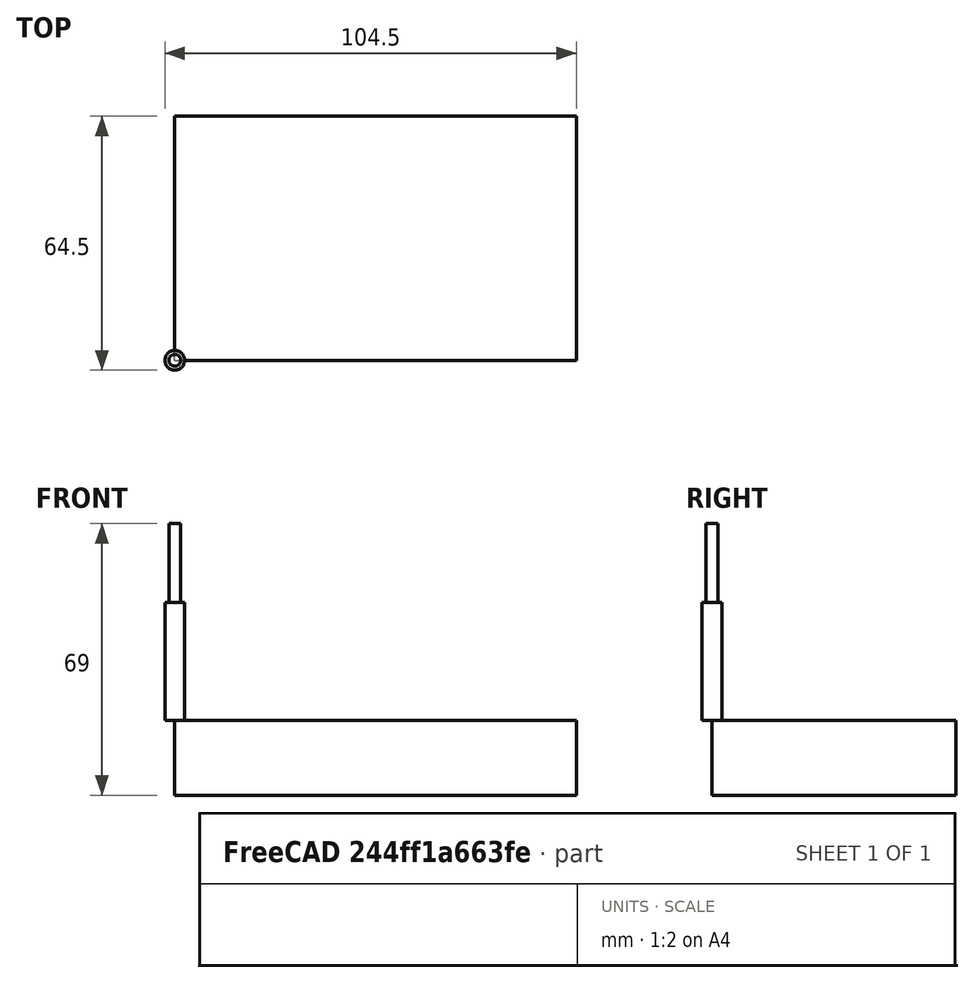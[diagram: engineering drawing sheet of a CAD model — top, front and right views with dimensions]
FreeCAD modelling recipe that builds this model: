
FCSTD DOCUMENT  (FreeCAD 0.19R23546 (Git))
Label: Cylindres25mmx19mmX2
License: All rights reserved
LicenseURL: http://en.wikipedia.org/wiki/All_rights_reserved
objects: Path::FeaturePython×6, Part::FeaturePython×3, Sketcher::SketchObject×2, PartDesign::Pad×1, PartDesign::Pocket×1, PartDesign::Body×1, App::FeaturePython×1, App::DocumentObjectGroup×1, Path::FeatureCompoundPython×1, Mesh::FeaturePython×1
note: 12 computed .brp shape members not serialized (recipe doc carries the construction recipe); baked Part::Feature solids carry a one-line shape summary decoded from their .brp

FEATURE [Sketcher::SketchObject] Sketch
  MapMode = 5
  Support = -> [XY_Plane]
  sketch-geometry (4):
    g0: LineSegment StartX=0 StartY=60 StartZ=0 EndX=100 EndY=60 EndZ=0
    g1: LineSegment StartX=100 StartY=60 StartZ=0 EndX=100 EndY=0 EndZ=0
    g2: LineSegment StartX=100 StartY=0 StartZ=0 EndX=0 EndY=0 EndZ=0
    g3: LineSegment StartX=0 StartY=0 StartZ=0 EndX=0 EndY=60 EndZ=0
  constraints (10):
    c: Coincident(g0,g1)
    c: Coincident(g1,g2)
    c: Coincident(g2,g3)
    c: Coincident(g3,g0)
    c: Horizontal(g0)
    c: Horizontal(g2)
    c: Vertical(g1)
    c: Vertical(g3)
    c: PointOnObject(g0,g-2)
    c: PointOnObject(g1,g-1)
FEATURE [PartDesign::Pad] Pad
  Direction = (1,1,1)
  Length = 19
  Length2 = 100
  Profile = -> Sketch
  Type = 0
FEATURE [Sketcher::SketchObject] Sketch001
  MapMode = 5
  Placement = pos=(0,0,19) rot=(0,0,1;0rad)
  Support = -> [Pad]
  sketch-geometry (2):
    g0: Circle CenterX=25 CenterY=30 CenterZ=0 NormalX=0 NormalY=0 NormalZ=1 AngleXU=0 Radius=18.5
    g1: Circle CenterX=75 CenterY=30 CenterZ=0 NormalX=0 NormalY=0 NormalZ=1 AngleXU=0 Radius=18.5
  constraints (4):
    c: DistanceX(g-1,g0) = 25
    c: Diameter(g0) = 37
    c: DistanceX(g-1,g1) = 75
    c: Diameter(g1) = 37
FEATURE [PartDesign::Pocket] Pocket
  BaseFeature = -> Pad
  Length = 5
  Length2 = 100
  Profile = -> Sketch001
  Type = 1
FEATURE [PartDesign::Body] Body
  Group = -> [Sketch,Pad,Sketch001,Pocket]
  Origin = -> Origin
  Tip = -> Pocket
FEATURE [App::FeaturePython] SetupSheet  # Path/CAM operation (typed FeaturePython)
  ClearanceHeightExpression = OpStockZMax+SetupSheet.ClearanceHeightOffset
  ClearanceHeightOffset = 5
  CoolantMode = 0
  CoolantModes = None | Flood | Mist
  FinalDepthExpression = OpFinalDepth
  HorizRapid = 0
  SafeHeightExpression = OpStockZMax+SetupSheet.SafeHeightOffset
  SafeHeightOffset = 3
  StartDepthExpression = OpStartDepth
  StepDownExpression = OpToolDiameter
  VertRapid = 0
FEATURE [Part::FeaturePython] Clone  label="Model-Body"  # Draft clone (typed FeaturePython)
  AttacherType = Attacher::AttachEngine3D
  Fuse = false
  Objects = -> [Body]
  PathResource = Model
  Placement = pos=(1,1,-19) rot=(0,0,1;0rad)
  Scale = (1,1,1)
FEATURE [App::DocumentObjectGroup] Model
  Group = -> [Clone]
FEATURE [Part::FeaturePython] ToolBit  label="Endmill"  # Path/CAM toolbit (typed FeaturePython)
  BitShape = <path>
  CuttingEdgeHeight = 30
  Diameter = 6
  Length = 50
  ShankDiameter = 3
  ShapeName = endmill
FEATURE [Path::FeaturePython] TC__Default_Tool  label="TC: Default Tool"  # Path/CAM operation (typed FeaturePython)
  HorizFeed = 0
  HorizRapid = 0
  SpindleDir = 0
  SpindleSpeed = 0
  Tool = -> ToolBit
  ToolNumber = 1
  VertFeed = 0
  VertRapid = 0
  expr: VertRapid = SetupSheet.VertRapid
  expr: HorizRapid = SetupSheet.HorizRapid
FEATURE [Part::FeaturePython] Stock  # WARN: FeaturePython — macro-defined, semantics opaque (R4)
  Base = -> Model
  ExtXneg = 1
  ExtXpos = 1
  ExtYneg = 1
  ExtYpos = 1
  ExtZneg = 0
  ExtZpos = 0
  Placement = pos=(1,1,-19) rot=(0,0,1;0rad)
  StockType = FromBase
FEATURE [Path::FeaturePython] Profile  # Path/CAM operation (typed FeaturePython)
  Active = true
  AreaParams:
    Tolerance = 1e-07
    FitArcs = True
    Simplify = False
    CleanDistance = 0.0
    Accuracy = 0.01
    Unit = 1.0
    MinArcPoints = 4
    MaxArcPoints = 100
    ClipperScale = 10000000.0
    Fill = 0
    Coplanar = 0
    Reorient = True
    Outline = False
    Explode = False
    OpenMode = 0
    Deflection = 0.01
    SubjectFill = 0
    ClipFill = 0
    Offset = -3.0
    ExtraPass = 0
    Stepover = 0.0
    LastStepover = 0.0
    JoinType = 0
    EndType = 0
    MiterLimit = 2.0
    RoundPrecision = 0.0
    PocketMode = 0
    ToolRadius = 1.0
    PocketExtraOffset = 0.0
    PocketStepover = 0.0
    PocketLastStepover = 0.0
    FromCenter = False
    Angle = 45.0
    AngleShift = 0.0
    Shift = 0.0
    Thicken = False
    SectionCount = -1
    Stepdown = 1.0
    SectionOffset = 0.0
    SectionTolerance = 1e-06
    SectionMode = 2
    Project = False
  AttemptInverseAngle = true
  Base = -> [Clone]
  ClearanceHeight = 5
  CoolantMode = None
  CycleTime = Erreur de temps de cycle
  Direction = 1
  EnableRotation = 0
  ExpandProfile = 0
  ExpandProfileStepOver = 100
  FinalDepth = -19
  HandleMultipleFeatures = 1
  InverseAngle = false
  JoinType = 0
  LimitDepthToFace = true
  MiterLimit = 0.1
  OffsetExtra = 0
  OpFinalDepth = -19
  OpStartDepth = 0
  OpStockZMax = 0
  OpStockZMin = -19
  OpToolDiameter = 6
  PathParams = {'orientation': 0, 'feedrate': 0.0, 'feedrate_v': 0.0, 'verbose': True, 'resume_height': 3.0, 'retraction': 5.0, 'return_end': True, 'preamble': False, 'start': Vector (0.0, 0.0, 0.0)}
  ReverseDirection = false
  SafeHeight = 3
  Side = 1
  StartDepth = 0
  StartPoint = (0,0,0)
  StepDown = 3
  ToolController = -> TC__Default_Tool
  UseComp = true
  UseStartPoint = true
  processCircles = false
  processHoles = false
  processPerimeter = true
  expr: StartDepth = OpStartDepth
  expr: FinalDepth = OpFinalDepth
  expr: StepDown = 3
  expr: SafeHeight = OpStockZMax + SetupSheet.SafeHeightOffset
  expr: ClearanceHeight = OpStockZMax + SetupSheet.ClearanceHeightOffset
FEATURE [Path::FeaturePython] DressupTag  # Path/CAM operation (typed FeaturePython)
  Angle = 45
  Base = -> Profile
  Height = 9.5
  Positions = (4) [(15.9082,42.7625,0),(11.1697,26.4985,0),(38.2957,21.5652,0),(35.4348,43.2957,0)]
  Radius = 0
  SegmentationFactor = 50
  Width = 3.58
FEATURE [Path::FeaturePython] Profile001  # Path/CAM operation (typed FeaturePython)
  Active = true
  AreaParams:
    Tolerance = 1e-07
    FitArcs = True
    Simplify = False
    CleanDistance = 0.0
    Accuracy = 0.01
    Unit = 1.0
    MinArcPoints = 4
    MaxArcPoints = 100
    ClipperScale = 10000000.0
    Fill = 0
    Coplanar = 0
    Reorient = True
    Outline = False
    Explode = False
    OpenMode = 0
    Deflection = 0.01
    SubjectFill = 0
    ClipFill = 0
    Offset = -3.0
    ExtraPass = 0
    Stepover = 0.0
    LastStepover = 0.0
    JoinType = 0
    EndType = 0
    MiterLimit = 2.0
    RoundPrecision = 0.0
    PocketMode = 0
    ToolRadius = 1.0
    PocketExtraOffset = 0.0
    PocketStepover = 0.0
    PocketLastStepover = 0.0
    FromCenter = False
    Angle = 45.0
    AngleShift = 0.0
    Shift = 0.0
    Thicken = False
    SectionCount = -1
    Stepdown = 1.0
    SectionOffset = 0.0
    SectionTolerance = 1e-06
    SectionMode = 2
    Project = False
  AttemptInverseAngle = true
  Base = -> [Clone]
  ClearanceHeight = 5
  CoolantMode = None
  CycleTime = Erreur de temps de cycle
  Direction = 1
  EnableRotation = 0
  ExpandProfile = 0
  ExpandProfileStepOver = 100
  FinalDepth = -19
  HandleMultipleFeatures = 1
  InverseAngle = false
  JoinType = 0
  LimitDepthToFace = true
  MiterLimit = 0.1
  OffsetExtra = 0
  OpFinalDepth = -19
  OpStartDepth = 0
  OpStockZMax = 0
  OpStockZMin = -19
  OpToolDiameter = 6
  PathParams = {'orientation': 0, 'feedrate': 0.0, 'feedrate_v': 0.0, 'verbose': True, 'resume_height': 3.0, 'retraction': 5.0, 'return_end': True, 'preamble': False, 'start': Vector (0.0, 0.0, 0.0)}
  ReverseDirection = false
  SafeHeight = 3
  Side = 1
  StartDepth = 0
  StartPoint = (0,0,0)
  StepDown = 3
  ToolController = -> TC__Default_Tool
  UseComp = true
  UseStartPoint = true
  processCircles = false
  processHoles = false
  processPerimeter = true
  expr: StartDepth = OpStartDepth
  expr: FinalDepth = OpFinalDepth
  expr: StepDown = 3
  expr: SafeHeight = OpStockZMax + SetupSheet.SafeHeightOffset
  expr: ClearanceHeight = OpStockZMax + SetupSheet.ClearanceHeightOffset
FEATURE [Path::FeaturePython] DressupTag001  # Path/CAM operation (typed FeaturePython)
  Angle = 45
  Base = -> Profile001
  Height = 9.5
  Positions = (4) [(62.599,38.7854,0),(68.2146,17.599,0),(88.2957,21.5652,0),(85.4348,43.2957,0)]
  Radius = 0
  SegmentationFactor = 50
  Width = 2.83
FEATURE [Path::FeatureCompoundPython] Operations  # Path/CAM operation (typed FeaturePython)
  Group = -> [DressupTag,DressupTag001]
  UsePlacements = false
FEATURE [Path::FeaturePython] Job  # Path/CAM operation (typed FeaturePython)
  CycleTime = 00:00:00
  Fixtures = G54
  GeometryTolerance = 0.01
  LastPostProcessDate = 2021-04-13 11:56:57.248228
  LastPostProcessOutput = <userpath>/dev/CNC/MiscCNC/FixationsCNC/Cylindres25mmx19mmX2.gcode
  Model = -> Model
  Operations = -> Operations
  OrderOutputBy = 0
  PostProcessor = 13
  PostProcessorOutputFile = <userpath>/dev/CNC/MiscCNC/FixationsCNC/Cylindres25mmx19mmX2.gcode
  SetupSheet = -> SetupSheet
  SplitOutput = false
  Stock = -> Stock
  ToolController = -> [TC__Default_Tool]
FEATURE [Mesh::FeaturePython] CutMaterial  # WARN: FeaturePython — macro-defined, semantics opaque (R4)
note: 1 file-system path scrubbed to <path> (originals preserved in the JSON sidecar)
